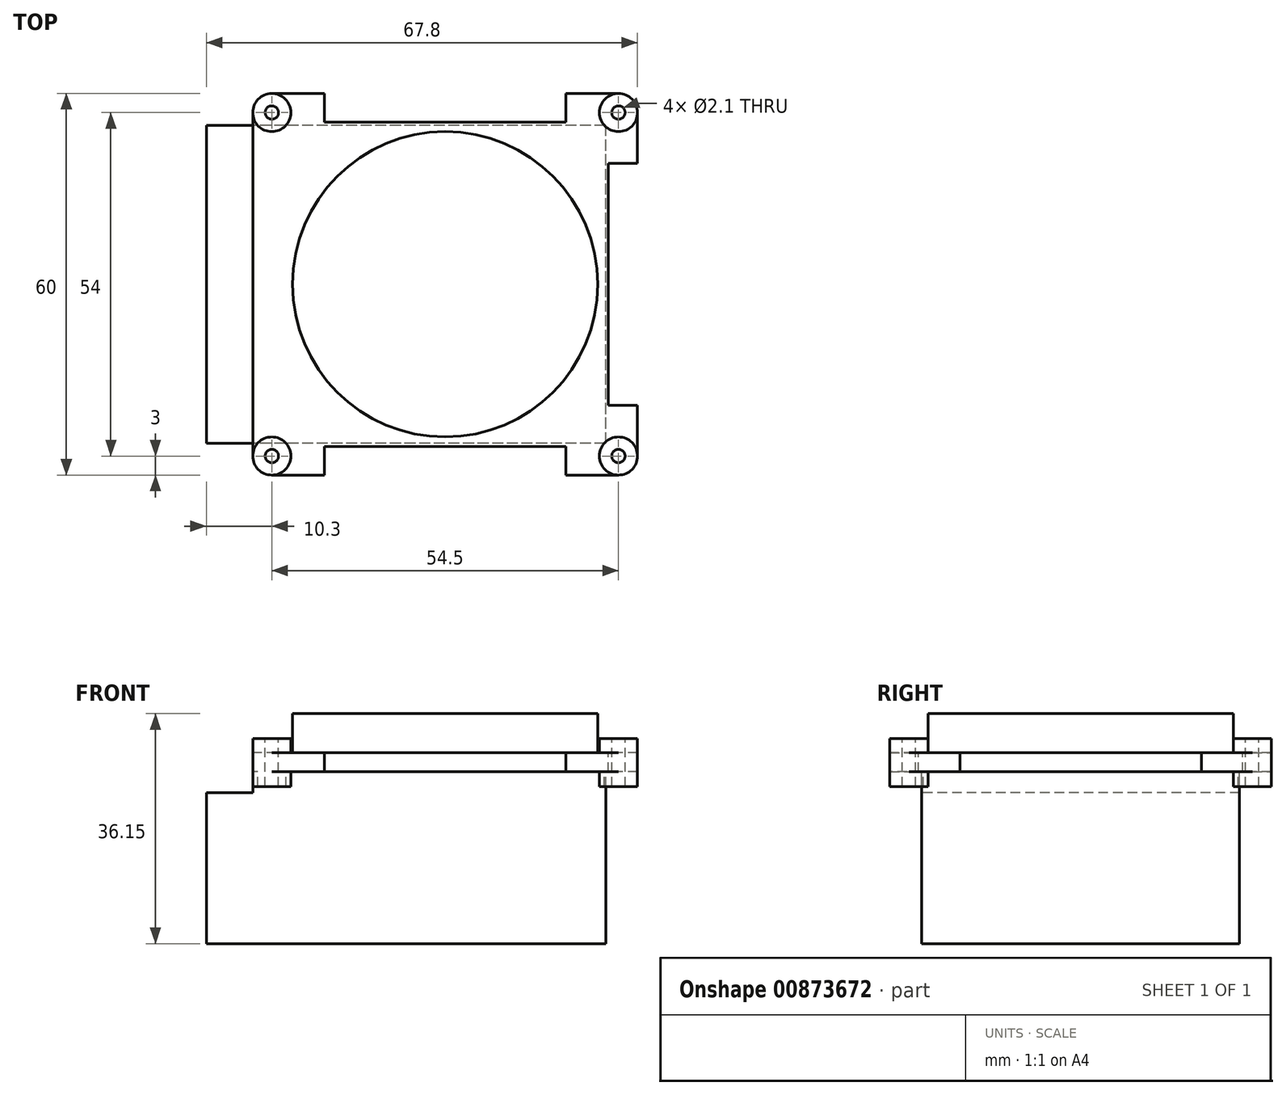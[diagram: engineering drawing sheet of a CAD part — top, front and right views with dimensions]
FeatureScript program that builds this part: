
annotation { "Feature Type Name" : "Feature", "Feature Type Description" : "" }
export const myFeature = defineFeature(function(context is Context, id is Id, definition is map)
    precondition{}
    {
        {
            var Q0;
            Q0=qCreatedBy(makeId("Top.planeOp"),FACE);
            var sketch = newSketch(context, id + "F0", { "sketchPlane" : qUnion([Q0])});
            skLineSegment(sketch, "E0.bottom", {"start": v(27.25, 30) * mm, "end": v(19, 30) * mm});
            skLineSegment(sketch, "E0.top", {"start": v(27.25, -30) * mm, "end": v(19, -30) * mm});
            skLineSegment(sketch, "E0.left", {"start": v(30.25, 27) * mm, "end": v(30.25, -27) * mm});
            skLineSegment(sketch, "E0.right", {"start": v(-30.25, 27) * mm, "end": v(-30.25, -27) * mm});
            skPoint(sketch, "E0.middle", {"position": v(0, 0) * mm});
            skCircle(sketch, "E1", {"center": v(0, 0) * mm, "radius": 24 * mm});
            skCircle(sketch, "E2", {"center": v(27.25, 27) * mm, "radius": 3 * mm});
            skCircle(sketch, "E3", {"center": v(-27.25, 27) * mm, "radius": 3 * mm});
            skCircle(sketch, "E4", {"center": v(-27.25, -27) * mm, "radius": 3 * mm});
            skCircle(sketch, "E5", {"center": v(27.25, -27) * mm, "radius": 3 * mm});
            skPoint(sketch, "E6.orphan", {"position": v(-30.25, 30) * mm});
            skPoint(sketch, "E7.orphan", {"position": v(30.25, 30) * mm});
            skPoint(sketch, "E8.orphan", {"position": v(30.25, -30) * mm});
            skPoint(sketch, "E9.orphan", {"position": v(-30.25, -30) * mm});
            skCircle(sketch, "E10", {"center": v(-27.25, 27) * mm, "radius": 1.05 * mm});
            skCircle(sketch, "E11", {"center": v(-27.25, -27) * mm, "radius": 1.05 * mm});
            skCircle(sketch, "E12", {"center": v(27.25, -27) * mm, "radius": 1.05 * mm});
            skCircle(sketch, "E13", {"center": v(27.25, 27) * mm, "radius": 1.05 * mm});
            skLineSegment(sketch, "E14.top", {"start": v(-19, 25.5) * mm, "end": v(19, 25.5) * mm});
            skLineSegment(sketch, "E14.left", {"start": v(-19, 30) * mm, "end": v(-19, 25.5) * mm});
            skLineSegment(sketch, "E14.right", {"start": v(19, 30) * mm, "end": v(19, 25.5) * mm});
            skLineSegment(sketch, "E15.trimOffspring", {"start": v(-19, 30) * mm, "end": v(-27.25, 30) * mm});
            skLineSegment(sketch, "E16.MirrorCS", {"start": v(-19, -30) * mm, "end": v(-19, -25.5) * mm});
            skLineSegment(sketch, "E17.MirrorCS", {"start": v(-19, -25.5) * mm, "end": v(19, -25.5) * mm});
            skLineSegment(sketch, "E18.MirrorCS", {"start": v(19, -30) * mm, "end": v(19, -25.5) * mm});
            skLineSegment(sketch, "E19.trimOffspring", {"start": v(-19, -30) * mm, "end": v(-27.25, -30) * mm});
            skLineSegment(sketch, "E20.bottom", {"start": v(30.25, -19) * mm, "end": v(25.65, -19) * mm});
            skLineSegment(sketch, "E20.top", {"start": v(30.25, 19) * mm, "end": v(25.65, 19) * mm});
            skLineSegment(sketch, "E20.left", {"start": v(30.25, -19) * mm, "end": v(30.25, 19) * mm});
            skLineSegment(sketch, "E20.right", {"start": v(25.65, -19) * mm, "end": v(25.65, 19) * mm});
            skSolve(sketch);
        }
        {
            var Q0;
            Q0=makeQuery(id+"F0.imprint","IMPRINT",FACE,{"disambiguationData":[TD([[makeQuery(id+"F0.imprint","IMPRINT",EDGE,{"derivedFrom":sQuery(id+"F0.wireOp",EDGE,"E1")}),1.0]])]});
            extrude(context, id + "F1", {"entities" : qUnion([Q0]), "depth" : 6.15 * mm, "offsetDistance" : 25 * mm});
        }
        {
            var Q0;
            Q0=makeQuery(id+"F0.imprint","IMPRINT",FACE,{"disambiguationData":[TD([[makeQuery(id+"F0.imprint","IMPRINT",EDGE,{"derivedFrom":sQuery(id+"F0.wireOp",EDGE,"E12")}),-1.0]])]});
            var Q1;
            Q1=makeQuery(id+"F0.imprint","IMPRINT",FACE,{"disambiguationData":[TD([[makeQuery(id+"F0.imprint","IMPRINT",EDGE,{"derivedFrom":sQuery(id+"F0.wireOp",EDGE,"E13")}),-1.0]])]});
            var Q2;
            Q2=makeQuery(id+"F0.imprint","IMPRINT",FACE,{"disambiguationData":[TD([[makeQuery(id+"F0.imprint","IMPRINT",EDGE,{"derivedFrom":sQuery(id+"F0.wireOp",EDGE,"E10")}),-1.0]])]});
            var Q3;
            Q3=makeQuery(id+"F0.imprint","IMPRINT",FACE,{"disambiguationData":[TD([[makeQuery(id+"F0.imprint","IMPRINT",EDGE,{"derivedFrom":sQuery(id+"F0.wireOp",EDGE,"E11")}),-1.0]])]});
            extrude(context, id + "F2", {"entities" : qUnion([Q0, Q1, Q2, Q3]), "depth" : 2.25 * mm, "offsetDistance" : 25 * mm});
        }
        {
            var Q0;
            Q0=makeQuery(id+"F0.imprint","IMPRINT",FACE,{"disambiguationData":[TD([[makeQuery(id+"F0.imprint","IMPRINT",EDGE,{"derivedFrom":sQuery(id+"F0.wireOp",EDGE,"E11")}),-1.0]])]});
            var Q1;
            Q1=makeQuery(id+"F0.imprint","IMPRINT",FACE,{"disambiguationData":[TD([[makeQuery(id+"F0.imprint","IMPRINT",EDGE,{"derivedFrom":sQuery(id+"F0.wireOp",EDGE,"E10")}),-1.0]])]});
            var Q2;
            Q2=makeQuery(id+"F0.imprint","IMPRINT",FACE,{"disambiguationData":[TD([[makeQuery(id+"F0.imprint","IMPRINT",EDGE,{"derivedFrom":sQuery(id+"F0.wireOp",EDGE,"E12")}),-1.0]])]});
            var Q3;
            Q3=makeQuery(id+"F0.imprint","IMPRINT",FACE,{"disambiguationData":[TD([[makeQuery(id+"F0.imprint","IMPRINT",EDGE,{"derivedFrom":sQuery(id+"F0.wireOp",EDGE,"E13")}),-1.0]])]});
            extrude(context, id + "F3", {"entities" : qUnion([Q0, Q1, Q2, Q3]), "oppositeDirection" : true, "depth" : 5.3 * mm, "offsetDistance" : 25 * mm});
        }
        {
            var Q0;
            {var subQ6=sQuery(id+"F0.wireOp",EDGE,"E0.bottom");Q0=makeQuery(id+"F0.imprint","IMPRINT",FACE,{"disambiguationData":[TD([[makeQuery(id+"F0.imprint","IMPRINT",EDGE,{"derivedFrom":subQ6}),1.0]])]});}
            extrude(context, id + "F4", {"entities" : qUnion([Q0]), "oppositeDirection" : true, "depth" : 3 * mm, "offsetDistance" : 25 * mm});
        }
        {
            var Q0;
            Q0=makeQuery(id+"F4.opExtrude","SWEPT_BODY",BODY,{"disambiguationData":[OSD([sQuery(id+"F0.wireOp",EDGE,"E0.bottom"),sQuery(id+"F0.wireOp",EDGE,"E0.top"),sQuery(id+"F0.wireOp",EDGE,"E0.left"),sQuery(id+"F0.wireOp",EDGE,"E0.right"),sQuery(id+"F0.wireOp",EDGE,"E1"),sQuery(id+"F0.wireOp",EDGE,"E2"),sQuery(id+"F0.wireOp",EDGE,"E3"),sQuery(id+"F0.wireOp",EDGE,"E4"),sQuery(id+"F0.wireOp",EDGE,"E5"),sQuery(id+"F0.wireOp",EDGE,"E14.top"),sQuery(id+"F0.wireOp",EDGE,"E14.left"),sQuery(id+"F0.wireOp",EDGE,"E14.right"),sQuery(id+"F0.wireOp",EDGE,"E15.trimOffspring"),sQuery(id+"F0.wireOp",EDGE,"E16.MirrorCS"),sQuery(id+"F0.wireOp",EDGE,"E17.MirrorCS"),sQuery(id+"F0.wireOp",EDGE,"E18.MirrorCS"),sQuery(id+"F0.wireOp",EDGE,"E19.trimOffspring")])]});
            var Q1;
            Q1=makeQuery(id+"F3.opExtrude","SWEPT_BODY",BODY,{"disambiguationData":[OSD([sQuery(id+"F0.wireOp",EDGE,"E5"),sQuery(id+"F0.wireOp",EDGE,"E12")])]});
            var Q2;
            Q2=makeQuery(id+"F3.opExtrude","SWEPT_BODY",BODY,{"disambiguationData":[OSD([sQuery(id+"F0.wireOp",EDGE,"E4"),sQuery(id+"F0.wireOp",EDGE,"E11")])]});
            var Q3;
            Q3=makeQuery(id+"F3.opExtrude","SWEPT_BODY",BODY,{"disambiguationData":[OSD([sQuery(id+"F0.wireOp",EDGE,"E3"),sQuery(id+"F0.wireOp",EDGE,"E10")])]});
            var Q4;
            Q4=makeQuery(id+"F3.opExtrude","SWEPT_BODY",BODY,{"disambiguationData":[OSD([sQuery(id+"F0.wireOp",EDGE,"E2"),sQuery(id+"F0.wireOp",EDGE,"E13")])]});
            var Q5;
            Q5=makeQuery(id+"F2.opExtrude","SWEPT_BODY",BODY,{"disambiguationData":[OSD([sQuery(id+"F0.wireOp",EDGE,"E5"),sQuery(id+"F0.wireOp",EDGE,"E12")])]});
            var Q6;
            Q6=makeQuery(id+"F2.opExtrude","SWEPT_BODY",BODY,{"disambiguationData":[OSD([sQuery(id+"F0.wireOp",EDGE,"E4"),sQuery(id+"F0.wireOp",EDGE,"E11")])]});
            var Q7;
            Q7=makeQuery(id+"F2.opExtrude","SWEPT_BODY",BODY,{"disambiguationData":[OSD([sQuery(id+"F0.wireOp",EDGE,"E3"),sQuery(id+"F0.wireOp",EDGE,"E10")])]});
            var Q8;
            Q8=makeQuery(id+"F2.opExtrude","SWEPT_BODY",BODY,{"disambiguationData":[OSD([sQuery(id+"F0.wireOp",EDGE,"E2"),sQuery(id+"F0.wireOp",EDGE,"E13")])]});
            var Q9;
            Q9=makeQuery(id+"F1.opExtrude","SWEPT_BODY",BODY,{"disambiguationData":[OSD([sQuery(id+"F0.wireOp",EDGE,"E1")])]});
            booleanBodies(context, id + "F5", {"operationType" : BooleanOperationType.UNION, "tools" : qUnion([Q0, Q1, Q2, Q3, Q4, Q5, Q6, Q7, Q8, Q9])});
        }
        {
            var Q0;
            Q0=makeQuery(id+"F0.imprint","IMPRINT",FACE,{"disambiguationData":[TD([[makeQuery(id+"F0.imprint","IMPRINT",EDGE,{"derivedFrom":sQuery(id+"F0.wireOp",EDGE,"E1")}),1.0]])]});
            var sketch = newSketch(context, id + "F6", { "sketchPlane" : qUnion([Q0])});
            skLineSegment(sketch, "E21.bottom", {"start": v(25.25, -25) * mm, "end": v(-30.25, -25) * mm});
            skLineSegment(sketch, "E21.top", {"start": v(25.25, 25) * mm, "end": v(-30.25, 25) * mm});
            skLineSegment(sketch, "E21.left", {"start": v(25.25, -25) * mm, "end": v(25.25, 25) * mm});
            skLineSegment(sketch, "E21.right", {"start": v(-30.25, -25) * mm, "end": v(-30.25, 25) * mm});
            skSolve(sketch);
        }
        {
            var Q0;
            Q0=qSketchRegion(id+"F6",true);
            extrude(context, id + "F7", {"entities" : qUnion([Q0]), "oppositeDirection" : true, "depth" : 30 * mm, "offsetDistance" : 25 * mm});
        }
        {
            var Q0;
            Q0=makeQuery(id+"F4.opExtrude","SWEPT_BODY",BODY,{"disambiguationData":[OSD([sQuery(id+"F0.wireOp",EDGE,"E0.bottom"),sQuery(id+"F0.wireOp",EDGE,"E0.top"),sQuery(id+"F0.wireOp",EDGE,"E0.left"),sQuery(id+"F0.wireOp",EDGE,"E0.right"),sQuery(id+"F0.wireOp",EDGE,"E1"),sQuery(id+"F0.wireOp",EDGE,"E2"),sQuery(id+"F0.wireOp",EDGE,"E3"),sQuery(id+"F0.wireOp",EDGE,"E4"),sQuery(id+"F0.wireOp",EDGE,"E5"),sQuery(id+"F0.wireOp",EDGE,"E14.top"),sQuery(id+"F0.wireOp",EDGE,"E14.left"),sQuery(id+"F0.wireOp",EDGE,"E14.right"),sQuery(id+"F0.wireOp",EDGE,"E15.trimOffspring"),sQuery(id+"F0.wireOp",EDGE,"E16.MirrorCS"),sQuery(id+"F0.wireOp",EDGE,"E17.MirrorCS"),sQuery(id+"F0.wireOp",EDGE,"E18.MirrorCS"),sQuery(id+"F0.wireOp",EDGE,"E19.trimOffspring")])]});
            var Q1;
            {var subQ0=sQuery(id+"F0.wireOp",EDGE,"E5");var subQ1=sQuery(id+"F0.wireOp",EDGE,"E4");var subQ2=sQuery(id+"F0.wireOp",EDGE,"E3");var subQ3=sQuery(id+"F0.wireOp",EDGE,"E2");var subQ4=sQuery(id+"F0.wireOp",EDGE,"E1");var subQ5=sQuery(id+"F0.wireOp",EDGE,"E12");var subQ6=sQuery(id+"F0.wireOp",EDGE,"E11");var subQ7=sQuery(id+"F0.wireOp",EDGE,"E10");var subQ8=sQuery(id+"F0.wireOp",EDGE,"E13");Q1=makeQuery(id+"F5.opBoolean","MERGE",BODY,{"derivedFrom":[makeQuery(id+"F1.opExtrude","SWEPT_BODY",BODY,{"disambiguationData":[OSD([subQ4])]}),makeQuery(id+"F2.opExtrude","SWEPT_BODY",BODY,{"disambiguationData":[OSD([subQ3,subQ8])]}),makeQuery(id+"F2.opExtrude","SWEPT_BODY",BODY,{"disambiguationData":[OSD([subQ2,subQ7])]}),makeQuery(id+"F2.opExtrude","SWEPT_BODY",BODY,{"disambiguationData":[OSD([subQ1,subQ6])]}),makeQuery(id+"F2.opExtrude","SWEPT_BODY",BODY,{"disambiguationData":[OSD([subQ0,subQ5])]}),makeQuery(id+"F3.opExtrude","SWEPT_BODY",BODY,{"disambiguationData":[OSD([subQ3,subQ8])]}),makeQuery(id+"F3.opExtrude","SWEPT_BODY",BODY,{"disambiguationData":[OSD([subQ2,subQ7])]}),makeQuery(id+"F3.opExtrude","SWEPT_BODY",BODY,{"disambiguationData":[OSD([subQ1,subQ6])]}),makeQuery(id+"F3.opExtrude","SWEPT_BODY",BODY,{"disambiguationData":[OSD([subQ0,subQ5])]}),makeQuery(id+"F4.opExtrude","SWEPT_BODY",BODY,{"disambiguationData":[OSD([sQuery(id+"F0.wireOp",EDGE,"E0.bottom"),sQuery(id+"F0.wireOp",EDGE,"E0.top"),sQuery(id+"F0.wireOp",EDGE,"E0.left"),sQuery(id+"F0.wireOp",EDGE,"E0.right"),subQ4,subQ3,subQ2,subQ1,subQ0,sQuery(id+"F0.wireOp",EDGE,"E14.top"),sQuery(id+"F0.wireOp",EDGE,"E14.left"),sQuery(id+"F0.wireOp",EDGE,"E14.right"),sQuery(id+"F0.wireOp",EDGE,"E15.trimOffspring"),sQuery(id+"F0.wireOp",EDGE,"E16.MirrorCS"),sQuery(id+"F0.wireOp",EDGE,"E17.MirrorCS"),sQuery(id+"F0.wireOp",EDGE,"E18.MirrorCS"),sQuery(id+"F0.wireOp",EDGE,"E19.trimOffspring")])]})]});}
            var Q2;
            Q2=makeQuery(id+"F7.opExtrude","SWEPT_BODY",BODY,{"disambiguationData":[OSD([sQuery(id+"F6.wireOp",EDGE,"E21.bottom"),sQuery(id+"F6.wireOp",EDGE,"E21.top"),sQuery(id+"F6.wireOp",EDGE,"E21.left"),sQuery(id+"F6.wireOp",EDGE,"E21.right")])]});
            booleanBodies(context, id + "F8", {"operationType" : BooleanOperationType.UNION, "tools" : qUnion([Q0, Q1, Q2])});
        }
        {
            var Q0;
            Q0=makeQuery(id+"F8.opBoolean","MERGE",FACE,{"derivedFrom":[makeQuery(id+"F4.opExtrude","SWEPT_FACE",FACE,{"disambiguationData":[OSD([sQuery(id+"F0.wireOp",EDGE,"E0.right")])]}),makeQuery(id+"F7.opExtrude","SWEPT_FACE",FACE,{"disambiguationData":[OSD([sQuery(id+"F6.wireOp",EDGE,"E21.right")])]})]});
            var sketch = newSketch(context, id + "F9", { "sketchPlane" : qUnion([Q0])});
            skLineSegment(sketch, "E22.bottom", {"start": v(-25, -30) * mm, "end": v(25, -30) * mm});
            skLineSegment(sketch, "E22.top", {"start": v(-25, -6.3) * mm, "end": v(25, -6.3) * mm});
            skLineSegment(sketch, "E22.left", {"start": v(-25, -30) * mm, "end": v(-25, -6.3) * mm});
            skLineSegment(sketch, "E22.right", {"start": v(25, -30) * mm, "end": v(25, -6.3) * mm});
            skSolve(sketch);
        }
        {
            var Q0;
            Q0=qSketchRegion(id+"F9",true);
            extrude(context, id + "F10", {"entities" : qUnion([Q0]), "operationType" : NewBodyOperationType.ADD, "depth" : 7.3 * mm, "offsetDistance" : 25 * mm});
        }
    });
